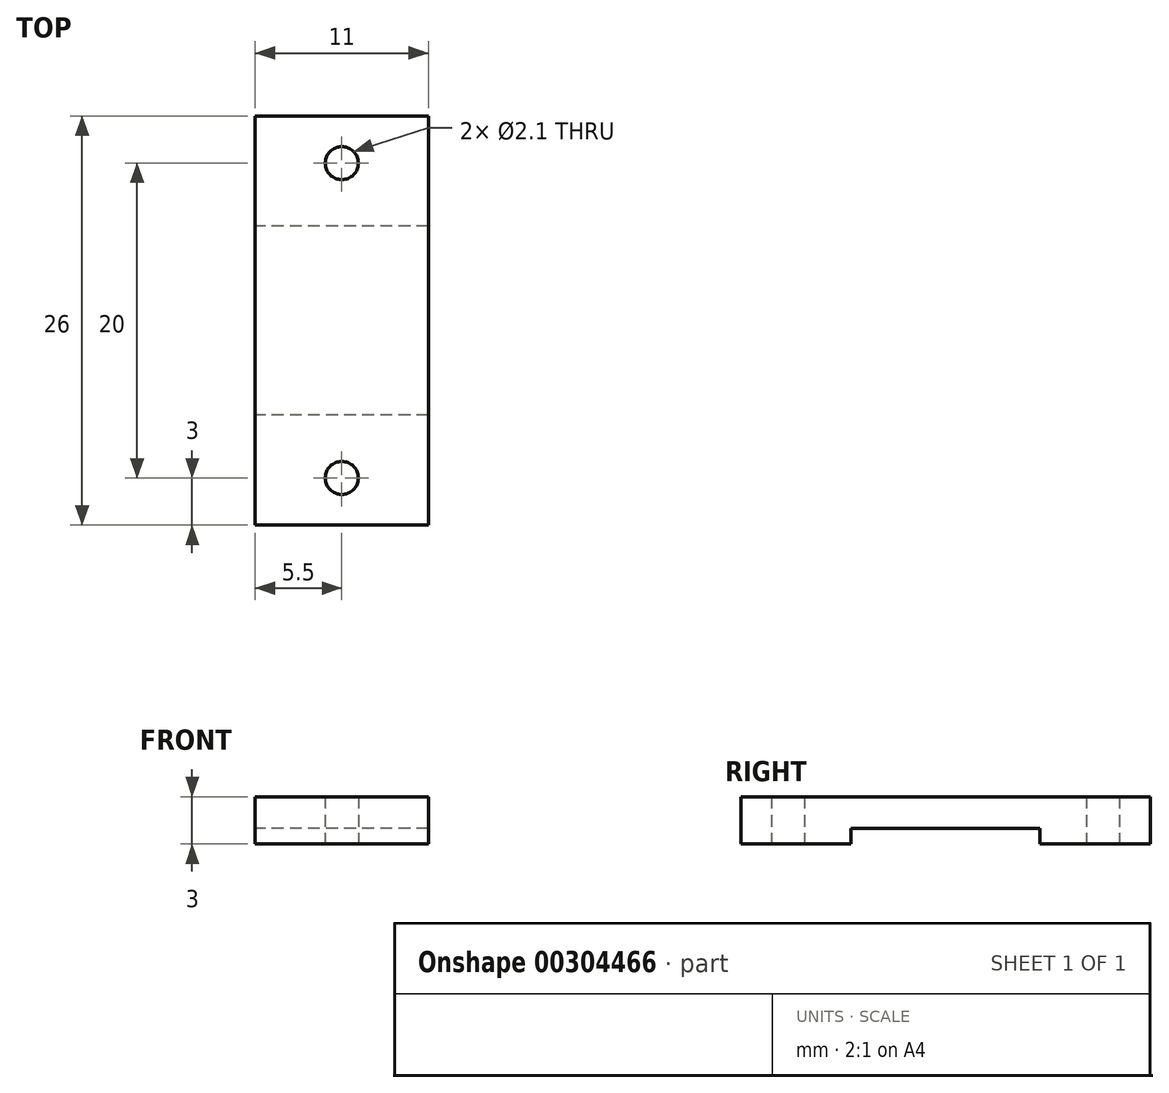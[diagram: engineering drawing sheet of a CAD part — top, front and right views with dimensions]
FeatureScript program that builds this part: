
annotation { "Feature Type Name" : "Feature", "Feature Type Description" : "" }
export const myFeature = defineFeature(function(context is Context, id is Id, definition is map)
    precondition{}
    {
        {
            var Q0;
            Q0=qCreatedBy(makeId("Top.planeOp"),FACE);
            var sketch = newSketch(context, id + "F0", { "sketchPlane" : qUnion([Q0])});
            skLineSegment(sketch, "E0.bottom", {"start": v(5.5, -13) * mm, "end": v(-5.5, -13) * mm});
            skLineSegment(sketch, "E0.top", {"start": v(5.5, 13) * mm, "end": v(-5.5, 13) * mm});
            skLineSegment(sketch, "E0.left", {"start": v(5.5, -13) * mm, "end": v(5.5, 13) * mm});
            skLineSegment(sketch, "E0.right", {"start": v(-5.5, -13) * mm, "end": v(-5.5, 13) * mm});
            skPoint(sketch, "E0.middle", {"position": v(0, 0) * mm});
            skSolve(sketch);
        }
        {
            var Q0;
            Q0 = qSketchRegion(id + "F0", true);
            extrude(context, id + "F1", {"entities" : qUnion([Q0]), "depth" : 3 * mm});
        }
        {
            var Q0;
            Q0=makeQuery(id+"F1.opExtrude","CAP_FACE",FACE,{"disambiguationData":[OSD([sQuery(id+"F0.wireOp",EDGE,"E0.bottom"),sQuery(id+"F0.wireOp",EDGE,"E0.top"),sQuery(id+"F0.wireOp",EDGE,"E0.left"),sQuery(id+"F0.wireOp",EDGE,"E0.right")])],"isStart":true});
            var sketch = newSketch(context, id + "F2", { "sketchPlane" : qUnion([Q0])});
            skLineSegment(sketch, "E1.bottom", {"start": v(5.5, -6) * mm, "end": v(-5.5, -6) * mm});
            skLineSegment(sketch, "E1.top", {"start": v(5.5, 6) * mm, "end": v(-5.5, 6) * mm});
            skLineSegment(sketch, "E1.left", {"start": v(5.5, -6) * mm, "end": v(5.5, 6) * mm});
            skLineSegment(sketch, "E1.right", {"start": v(-5.5, -6) * mm, "end": v(-5.5, 6) * mm});
            skPoint(sketch, "E1.middle", {"position": v(0, 0) * mm});
            skSolve(sketch);
        }
        {
            var Q0;
            Q0 = qSketchRegion(id + "F2", true);
            extrude(context, id + "F3", {"entities" : qUnion([Q0]), "operationType" : NewBodyOperationType.REMOVE, "oppositeDirection" : true, "depth" : 1 * mm});
        }
        {
            var Q0;
            Q0=makeQuery(id+"F1.opExtrude","CAP_FACE",FACE,{"disambiguationData":[OSD([sQuery(id+"F0.wireOp",EDGE,"E0.bottom"),sQuery(id+"F0.wireOp",EDGE,"E0.top"),sQuery(id+"F0.wireOp",EDGE,"E0.left"),sQuery(id+"F0.wireOp",EDGE,"E0.right")])],"isStart":false});
            var sketch = newSketch(context, id + "F4", { "sketchPlane" : qUnion([Q0])});
            skPoint(sketch, "E2", {"position": v(0, 10) * mm});
            skPoint(sketch, "E3", {"position": v(0, -10) * mm});
            skSolve(sketch);
        }
        {
            var Q0;
            Q0=sQuery(id+"F4.wireOp",VERTEX,"E2");
            var Q1;
            Q1=sQuery(id+"F4.wireOp",VERTEX,"E3");
            var Q2;
            Q2=makeQuery(id+"F1.opExtrude","SWEPT_BODY",BODY,{"disambiguationData":[OSD([sQuery(id+"F0.wireOp",EDGE,"E0.bottom"),sQuery(id+"F0.wireOp",EDGE,"E0.top"),sQuery(id+"F0.wireOp",EDGE,"E0.left"),sQuery(id+"F0.wireOp",EDGE,"E0.right")])]});
            hole(context, id + "F5", {"style" : HoleStyle.SIMPLE, "endStyle" : HoleEndStyle.THROUGH, "holeDiameter" : 2.1 * mm, "tappedDepth" : 12 * mm, "tapClearance" : 3, "locations" : qUnion([Q0, Q1]), "scope" : qUnion([Q2]), "startStyle" : HoleStartStyle.PART});
        }
    });
